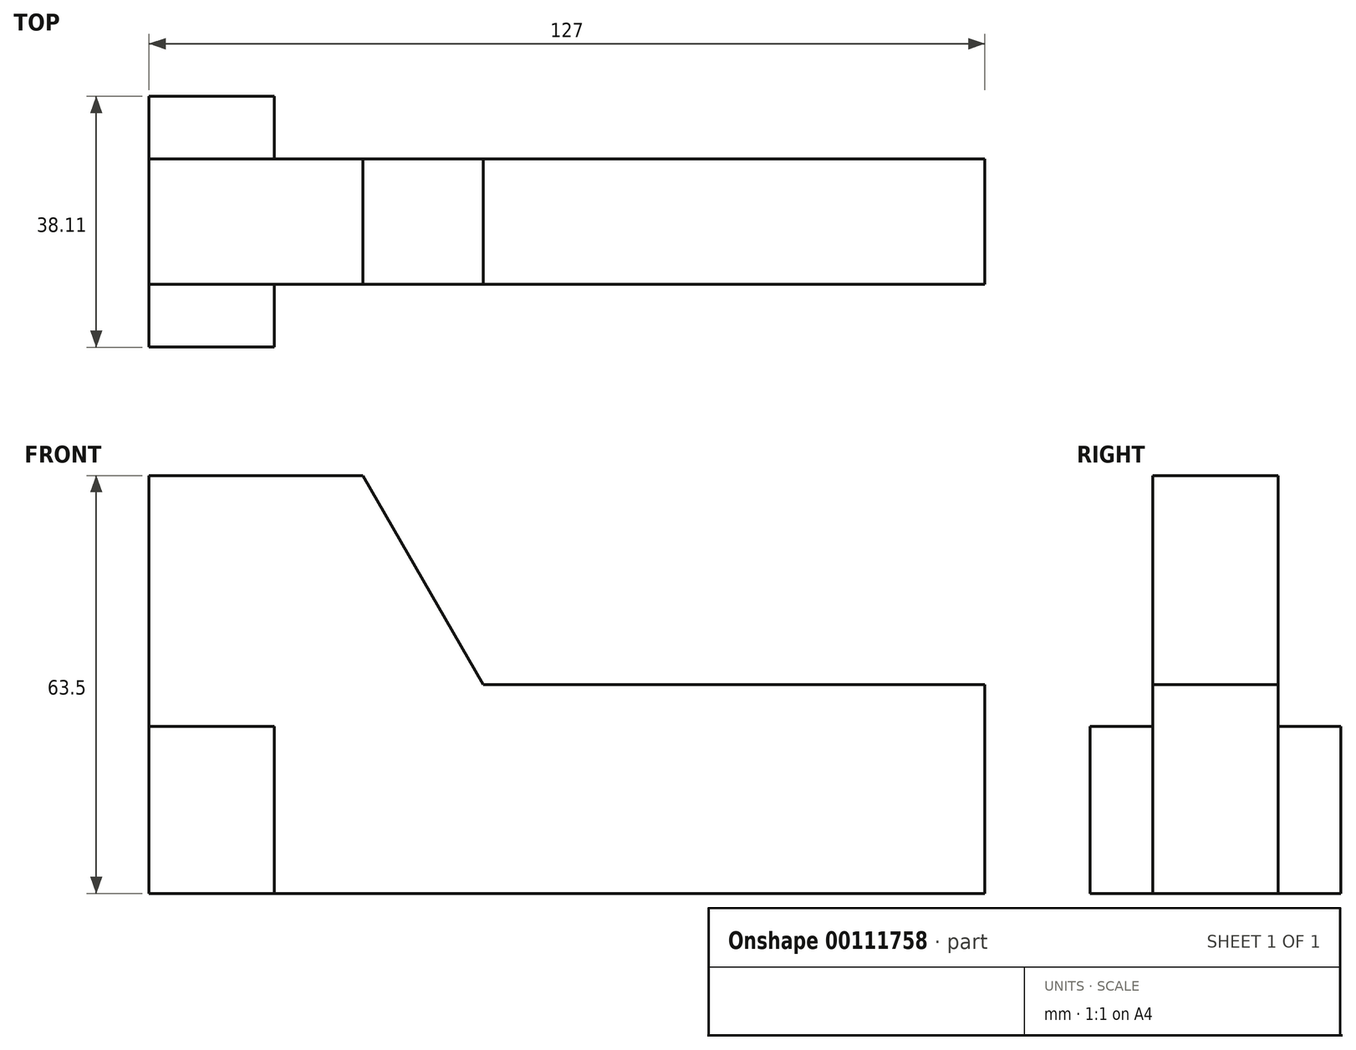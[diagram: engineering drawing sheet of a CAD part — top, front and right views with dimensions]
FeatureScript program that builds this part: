
annotation { "Feature Type Name" : "Feature", "Feature Type Description" : "" }
export const myFeature = defineFeature(function(context is Context, id is Id, definition is map)
    precondition{}
    {
        {
            var Q0;
            Q0=qCreatedBy(makeId("Front.planeOp"),FACE);
            var sketch = newSketch(context, id + "F0", { "sketchPlane" : qUnion([Q0])});
            skLineSegment(sketch, "E0.bottom", {"start": v(-74.08, 20.82) * mm, "end": v(52.92, 20.82) * mm});
            skLineSegment(sketch, "E0.top", {"start": v(-74.08, -42.68) * mm, "end": v(52.92, -42.68) * mm});
            skLineSegment(sketch, "E0.left", {"start": v(-74.08, 20.82) * mm, "end": v(-74.08, -42.68) * mm});
            skLineSegment(sketch, "E0.right", {"start": v(52.92, 20.82) * mm, "end": v(52.92, -42.68) * mm});
            skSolve(sketch);
        }
        {
            var Q0;
            Q0 = qSketchRegion(id + "F0", true);
            extrude(context, id + "F1", {"entities" : qUnion([Q0]), "oppositeDirection" : true, "depth" : 19.05 * mm});
        }
        {
            var Q0;
            Q0=makeQuery(id+"F1.opExtrude","SWEPT_FACE",FACE,{"disambiguationData":[OSD([sQuery(id+"F0.wireOp",EDGE,"E0.bottom")])]});
            var sketch = newSketch(context, id + "F2", { "sketchPlane" : qUnion([Q0])});
            skLineSegment(sketch, "E1.bottom", {"start": v(52.92, 19.05) * mm, "end": v(-23.28, 19.05) * mm});
            skLineSegment(sketch, "E1.top", {"start": v(52.92, 0) * mm, "end": v(-23.28, 0) * mm});
            skLineSegment(sketch, "E1.left", {"start": v(52.92, 19.05) * mm, "end": v(52.92, 0) * mm});
            skLineSegment(sketch, "E1.right", {"start": v(-23.28, 19.05) * mm, "end": v(-23.28, 0) * mm});
            skSolve(sketch);
        }
        {
            var Q0;
            Q0 = qSketchRegion(id + "F2", true);
            extrude(context, id + "F3", {"entities" : qUnion([Q0]), "operationType" : NewBodyOperationType.REMOVE, "oppositeDirection" : true, "depth" : 31.75 * mm});
        }
        {
            var Q0;
            Q0=makeQuery(id+"F1.opExtrude","CAP_FACE",FACE,{"disambiguationData":[OSD([sQuery(id+"F0.wireOp",EDGE,"E0.bottom"),sQuery(id+"F0.wireOp",EDGE,"E0.top"),sQuery(id+"F0.wireOp",EDGE,"E0.left"),sQuery(id+"F0.wireOp",EDGE,"E0.right")])],"isStart":true});
            var sketch = newSketch(context, id + "F4", { "sketchPlane" : qUnion([Q0])});
            skLineSegment(sketch, "E2", {"start": v(-23.28, -10.93) * mm, "end": v(-41.6, 20.82) * mm});
            skSolve(sketch);
        }
        {
            var Q0;
            Q0 = qSketchRegion(id + "F4", true);
            var Q1;
            {var subQ0=sQuery(id+"F4.wireOp",EDGE,"E2");Q1=makeQuery(id+"F4.imprint","IMPRINT",FACE,{"disambiguationData":[TD([[makeQuery(id+"F4.imprint","IMPRINT",EDGE,{"derivedFrom":subQ0}),-1.0]])]});}
            extrude(context, id + "F5", {"entities" : qUnion([Q0, Q1]), "operationType" : NewBodyOperationType.REMOVE, "oppositeDirection" : true, "depth" : 25.4 * mm});
        }
        {
            var Q0;
            Q0=makeQuery(id+"F1.opExtrude","CAP_FACE",FACE,{"disambiguationData":[OSD([sQuery(id+"F0.wireOp",EDGE,"E0.bottom"),sQuery(id+"F0.wireOp",EDGE,"E0.top"),sQuery(id+"F0.wireOp",EDGE,"E0.left"),sQuery(id+"F0.wireOp",EDGE,"E0.right")])],"isStart":true});
            var sketch = newSketch(context, id + "F6", { "sketchPlane" : qUnion([Q0])});
            skLineSegment(sketch, "E3.bottom", {"start": v(-74.08, -17.28) * mm, "end": v(-55.03, -17.28) * mm});
            skLineSegment(sketch, "E3.top", {"start": v(-74.08, -42.68) * mm, "end": v(-55.03, -42.68) * mm});
            skLineSegment(sketch, "E3.left", {"start": v(-74.08, -17.28) * mm, "end": v(-74.08, -42.68) * mm});
            skLineSegment(sketch, "E3.right", {"start": v(-55.03, -17.28) * mm, "end": v(-55.03, -42.68) * mm});
            skSolve(sketch);
        }
        {
            var Q0;
            Q0 = qSketchRegion(id + "F6", true);
            extrude(context, id + "F7", {"entities" : qUnion([Q0]), "operationType" : NewBodyOperationType.ADD, "depth" : 9.52 * mm, "hasSecondDirection" : true, "secondDirectionOppositeDirection" : true, "secondDirectionDepth" : 28.57 * mm});
        }
    });
